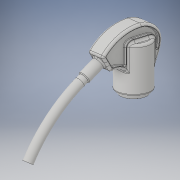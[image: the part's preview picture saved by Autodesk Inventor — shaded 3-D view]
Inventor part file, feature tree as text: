
AUTODESK INVENTOR PART (.ipt)
format: ipt  version: 2018 (Build 220112000, 112)  size: 887,808 bytes
history: native  units: mm
features: fillet x9, sketch x7, extrude x5, projected_geometry x2, revolve x1, plane x1, sweep x1
ambient origin geometry x8: Origin, YZ Plane, XZ Plane, XY Plane, X Axis, Y Axis, Z Axis, Center Point
bodies: Solid1 (feature_tree), Solid2 (feature_tree)
feature tree (26):
  revolve  "Revolution1"  [1 undecoded]
  extrude  "Extrusion1"  Depth=11.2mm
  fillet  "Fillet1"  Radius=1.69mm
  extrude  "Extrusion2"  Depth=5.69mm
  extrude  "Extrusion3"  Depth=1.5mm
  fillet  "Fillet2"  Radius=0.8mm
  fillet  "Fillet3"  Radius=0.25mm
  plane  "Work Plane1"
  sweep  "Sweep1"
  fillet  "Fillet4"  [1 undecoded]
  fillet  "Fillet5"  Radius=2.6mm
  sketch  "Sketch7"  dims[d21=8.5mm d22=4.0mm d23=0.8mm d24=6.0mm d25=0.0mm d26=3.6mm d27=3.0mm d28=6.0mm d29=0.0mm d30=0.5mm d31=0.25mm d32=0.0mm d33=0.0mm d34=0.8mm d35=0.8mm d36=0.2mm d37=0.4mm d38=1.0mm d39=0.0mm d40=0.2mm d41=0.1mm d42=1.0mm d43=0.0mm d44=0.1mm d45=0.2mm]
  extrude  "Extrusion4"  Depth=0.5mm
  fillet  "Fillet6"  Radius=20.0mm
  fillet  "Fillet7"  Radius=5.35mm
  extrude  "Extrusion5"  Depth=0.2mm
  fillet  "Fillet8"  Radius=0.8mm
  fillet  "Fillet9"  Radius=6.0mm
  sketch  "Sketch1"  dims[d0=2.87mm d1=3.87mm d2=5.29mm]
  sketch  "Sketch2"  dims[d3=15.4mm d4=11.2mm d5=1.69mm]
  sketch  "Sketch3"  dims[d6=3.7mm d7=5.69mm]
  sketch  "Sketch4"  dims[d8=2.85mm d9=1.5mm d10=0.8mm d11=0.25mm]
  sketch  "Sketch5"  dims[d12=0.5mm d13=0.25mm d14=90.0deg d15=2.6mm]
  sketch  "Sketch6"  dims[d16=1.22mm d17=0.0mm d18=0.5mm d19=20.0mm d20=5.35mm]
  projected_geometry  "Projected Loop1"
  projected_geometry  "Projected Loop2"
note: 2 required parameter values undecoded (feature->parameter linkage not recoverable at this tier; creation-order binding heuristic only, values carry confidence <= 0.55)